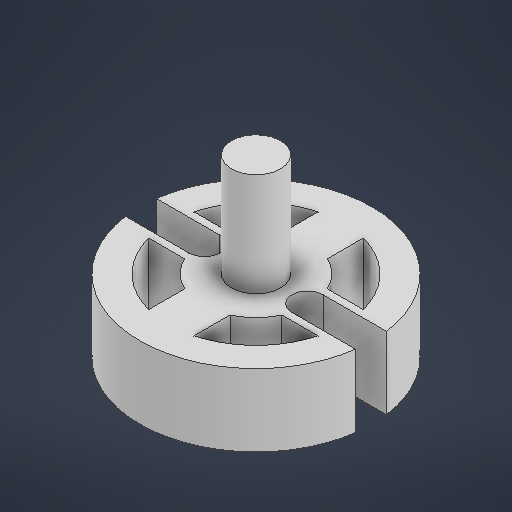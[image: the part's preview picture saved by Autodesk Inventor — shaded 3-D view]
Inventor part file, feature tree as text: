
AUTODESK INVENTOR PART (.ipt)
format: ipt  version: 2025.3 (Build 293356000, 356)  size: 284,160 bytes
history: native  units: mm
features: sketch x5, extrude x4, plane x2
ambient origin geometry x8: Origin, YZ Plane, XZ Plane, XY Plane, X Axis, Y Axis, Z Axis, Center Point
bodies: Solid1 (feature_tree)
feature tree (11):
  extrude  "Extrusion1"  Depth=9.5mm
  extrude  "Extrusion2"  Depth=14.0mm
  plane  "Work Plane3"
  extrude  "Extrusion4"  Depth=17.0mm
  plane  "Work Plane4"
  extrude  "Extrusion5"  Depth=14.0mm TaperAngle=0.0deg
  sketch  "Sketch1"  dims[d0=45.0mm d1=9.5mm]
  sketch  "Sketch2"  dims[d10=14.0mm d11=0.0mm d30=7.0mm]
  sketch  "Sketch Circular Pattern3"  dims[d31=6.981317mm d32=17.0mm]
  sketch  "Sketch4"  dims[d33=40.0mm d35=360.0deg d40=14.0mm d41=0.0mm]
  sketch  "Sketch6"  dims[d49=6.0mm d50=7.0mm d51=15.0mm d52=3.8mm d53=7.0mm d54=2.9mm d55=6.0mm d56=0.0mm d57=0.0mm d58=13.0mm d59=20.0mm d60=0.0mm d61=4.0mm d62=0.0mm]
